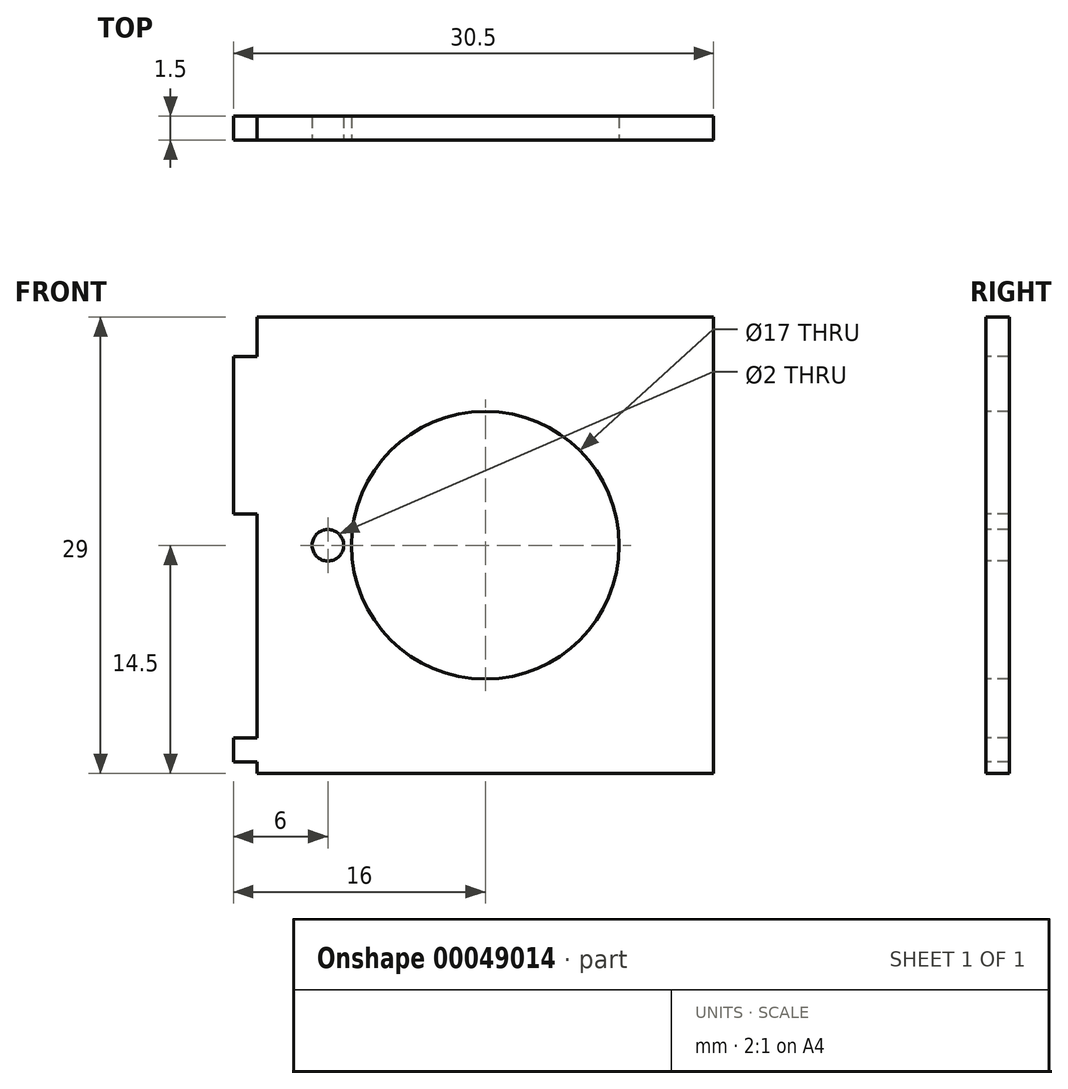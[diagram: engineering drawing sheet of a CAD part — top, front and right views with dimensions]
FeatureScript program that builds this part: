
annotation { "Feature Type Name" : "Feature", "Feature Type Description" : "" }
export const myFeature = defineFeature(function(context is Context, id is Id, definition is map)
    precondition{}
    {
        {
            var Q0;
            Q0=qCreatedBy(makeId("Front.planeOp"),FACE);
            var sketch = newSketch(context, id + "F0", { "sketchPlane" : qUnion([Q0])});
            skLineSegment(sketch, "E0.bottom", {"start": v(14.5, 14.5) * mm, "end": v(-14.5, 14.5) * mm});
            skLineSegment(sketch, "E0.top", {"start": v(14.5, -14.5) * mm, "end": v(-14.5, -14.5) * mm});
            skLineSegment(sketch, "E0.left", {"start": v(14.5, 14.5) * mm, "end": v(14.5, -14.5) * mm});
            skLineSegment(sketch, "E0.right", {"start": v(-14.5, 14.5) * mm, "end": v(-14.5, -14.5) * mm});
            skPoint(sketch, "E0.middle", {"position": v(0, 0) * mm});
            skSolve(sketch);
        }
        {
            var Q0;
            Q0 = qSketchRegion(id + "F0", true);
            extrude(context, id + "F1", {"entities" : qUnion([Q0]), "depth" : 1.5 * mm});
        }
        {
            var Q0;
            Q0=makeQuery(id+"F1.opExtrude","CAP_FACE",FACE,{"disambiguationData":[OSD([sQuery(id+"F0.wireOp",EDGE,"E0.bottom"),sQuery(id+"F0.wireOp",EDGE,"E0.top"),sQuery(id+"F0.wireOp",EDGE,"E0.left"),sQuery(id+"F0.wireOp",EDGE,"E0.right")])],"isStart":false});
            var sketch = newSketch(context, id + "F2", { "sketchPlane" : qUnion([Q0])});
            skCircle(sketch, "E1", {"center": v(0, 0) * mm, "radius": 8.5 * mm});
            skSolve(sketch);
        }
        {
            var Q0;
            Q0 = qSketchRegion(id + "F2", true);
            extrude(context, id + "F3", {"entities" : qUnion([Q0]), "operationType" : NewBodyOperationType.REMOVE, "endBound" : BoundingType.THROUGH_ALL, "oppositeDirection" : true, "depth" : 25 * mm});
        }
        {
            var Q0;
            Q0=makeQuery(id+"F1.opExtrude","CAP_FACE",FACE,{"disambiguationData":[OSD([sQuery(id+"F0.wireOp",EDGE,"E0.bottom"),sQuery(id+"F0.wireOp",EDGE,"E0.top"),sQuery(id+"F0.wireOp",EDGE,"E0.left"),sQuery(id+"F0.wireOp",EDGE,"E0.right")])],"isStart":false});
            var sketch = newSketch(context, id + "F4", { "sketchPlane" : qUnion([Q0])});
            skLineSegment(sketch, "E2", {"start": v(0, 0) * mm, "end": v(-10, 0) * mm, "construction": true});
            skCircle(sketch, "E3", {"center": v(-10, 0) * mm, "radius": 1 * mm});
            skSolve(sketch);
        }
        {
            var Q0;
            Q0 = qSketchRegion(id + "F4", true);
            extrude(context, id + "F5", {"entities" : qUnion([Q0]), "operationType" : NewBodyOperationType.REMOVE, "endBound" : BoundingType.THROUGH_ALL, "oppositeDirection" : true, "depth" : 25 * mm});
        }
        {
            var Q0;
            Q0=makeQuery(id+"F1.opExtrude","CAP_FACE",FACE,{"disambiguationData":[OSD([sQuery(id+"F0.wireOp",EDGE,"E0.bottom"),sQuery(id+"F0.wireOp",EDGE,"E0.top"),sQuery(id+"F0.wireOp",EDGE,"E0.left"),sQuery(id+"F0.wireOp",EDGE,"E0.right")])],"isStart":false});
            var sketch = newSketch(context, id + "F6", { "sketchPlane" : qUnion([Q0])});
            skLineSegment(sketch, "E4.bottom", {"start": v(-16, -13.75) * mm, "end": v(-14.5, -13.75) * mm});
            skLineSegment(sketch, "E4.top", {"start": v(-14.5, -12.25) * mm, "end": v(-16, -12.25) * mm});
            skLineSegment(sketch, "E4.left", {"start": v(-16, -13.75) * mm, "end": v(-16, -12.25) * mm});
            skLineSegment(sketch, "E4.right", {"start": v(-14.5, -13.75) * mm, "end": v(-14.5, -12.25) * mm});
            skLineSegment(sketch, "E5.bottom", {"start": v(-14.5, 2) * mm, "end": v(-16, 2) * mm});
            skLineSegment(sketch, "E5.top", {"start": v(-14.5, 12) * mm, "end": v(-16, 12) * mm});
            skLineSegment(sketch, "E5.left", {"start": v(-14.5, 2) * mm, "end": v(-14.5, 12) * mm});
            skLineSegment(sketch, "E5.right", {"start": v(-16, 2) * mm, "end": v(-16, 12) * mm});
            skSolve(sketch);
        }
        {
            var Q0;
            Q0 = qSketchRegion(id + "F6", true);
            extrude(context, id + "F7", {"entities" : qUnion([Q0]), "operationType" : NewBodyOperationType.ADD, "oppositeDirection" : true, "depth" : 1.5 * mm});
        }
    });
